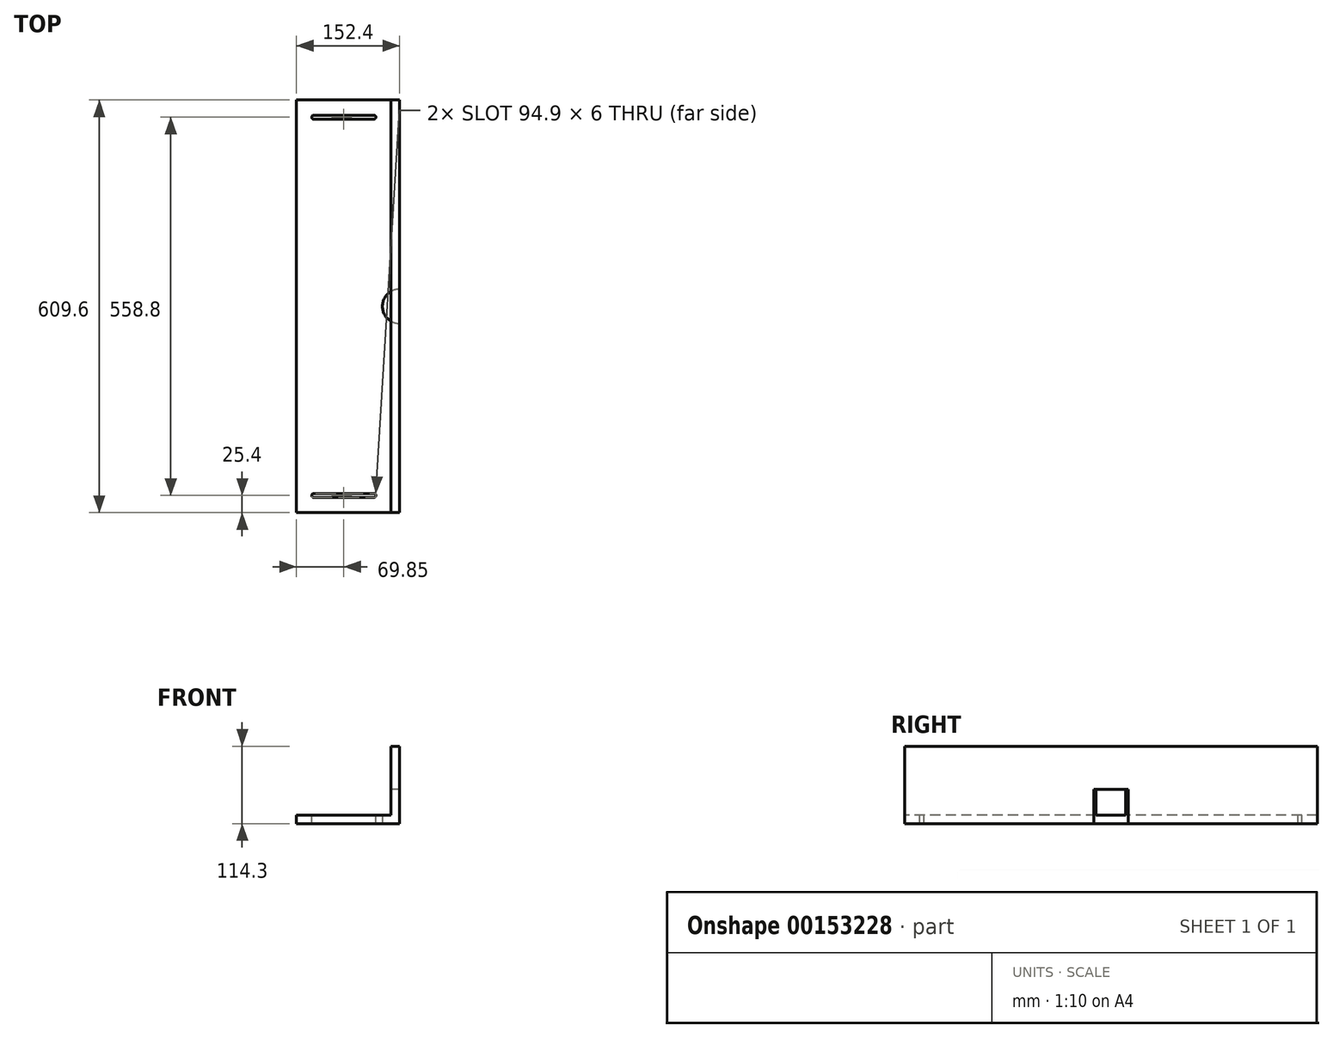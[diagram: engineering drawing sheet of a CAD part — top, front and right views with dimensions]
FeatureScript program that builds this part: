
annotation { "Feature Type Name" : "Feature", "Feature Type Description" : "" }
export const myFeature = defineFeature(function(context is Context, id is Id, definition is map)
    precondition{}
    {
        {
            var Q0;
            Q0=qCreatedBy(makeId("Top.planeOp"),FACE);
            var sketch = newSketch(context, id + "F0", { "sketchPlane" : qUnion([Q0])});
            skLineSegment(sketch, "E0.bottom", {"start": v(-152.4, 304.8) * mm, "end": v(0, 304.8) * mm});
            skLineSegment(sketch, "E0.top", {"start": v(-152.4, -304.8) * mm, "end": v(0, -304.8) * mm});
            skLineSegment(sketch, "E0.left", {"start": v(-152.4, 304.8) * mm, "end": v(-152.4, -304.8) * mm});
            skLineSegment(sketch, "E1", {"start": v(0, 304.8) * mm, "end": v(0, -304.8) * mm});
            skSolve(sketch);
        }
        {
            var Q0;
            Q0=makeQuery(id+"F0.imprint","IMPRINT",FACE,{"disambiguationData":[TD([[makeQuery(id+"F0.imprint","IMPRINT",EDGE,{"derivedFrom":sQuery(id+"F0.wireOp",EDGE,"E0.bottom")}),-1.0]])]});
            extrude(context, id + "F1", {"entities" : qUnion([Q0]), "depth" : 12.7 * mm});
        }
        {
            var Q0;
            Q0=makeQuery(id+"F1.opExtrude","CAP_FACE",FACE,{"disambiguationData":[OSD([sQuery(id+"F0.wireOp",EDGE,"E0.bottom"),sQuery(id+"F0.wireOp",EDGE,"E0.top"),sQuery(id+"F0.wireOp",EDGE,"E0.left"),sQuery(id+"F0.wireOp",EDGE,"E0.right"),sQuery(id+"F0.wireOp",EDGE,"2Zo1Db0u-jxeq-ltlI-ydCZ-03XNrdQAzi5M"),sQuery(id+"F0.wireOp",EDGE,"4c3afef6-3c96-4deb-abbf-9a2fc886915c.trimOffspring")])],"isStart":false});
            var sketch = newSketch(context, id + "F2", { "sketchPlane" : qUnion([Q0])});
            skLineSegment(sketch, "E2.bottom", {"start": v(0, 304.8) * mm, "end": v(-12.7, 304.8) * mm});
            skLineSegment(sketch, "E2.top", {"start": v(0, -304.8) * mm, "end": v(-12.7, -304.8) * mm});
            skLineSegment(sketch, "E2.left", {"start": v(0, 304.8) * mm, "end": v(0, -304.8) * mm});
            skLineSegment(sketch, "E2.right", {"start": v(-12.7, 304.8) * mm, "end": v(-12.7, -304.8) * mm});
            skSolve(sketch);
        }
        {
            var Q0;
            Q0 = qSketchRegion(id + "F2", true);
            extrude(context, id + "F3", {"entities" : qUnion([Q0]), "operationType" : NewBodyOperationType.ADD, "depth" : 101.6 * mm});
        }
        {
            var Q0;
            Q0=makeQuery(id+"F1.opExtrude","CAP_FACE",FACE,{"disambiguationData":[OSD([sQuery(id+"F0.wireOp",EDGE,"E0.bottom"),sQuery(id+"F0.wireOp",EDGE,"E0.top"),sQuery(id+"F0.wireOp",EDGE,"E0.left"),sQuery(id+"F0.wireOp",EDGE,"E1")])],"isStart":false});
            var sketch = newSketch(context, id + "F4", { "sketchPlane" : qUnion([Q0])});
            skLineSegment(sketch, "E3.bottom", {"start": v(-127, 282.4) * mm, "end": v(-38.1, 282.4) * mm});
            skLineSegment(sketch, "E3.top", {"start": v(-127, 276.4) * mm, "end": v(-38.1, 276.4) * mm});
            skLineSegment(sketch, "E4.bottom", {"start": v(-127, -276.4) * mm, "end": v(-38.1, -276.4) * mm});
            skLineSegment(sketch, "E4.top", {"start": v(-127, -282.4) * mm, "end": v(-38.1, -282.4) * mm});
            skArc(sketch, "E5", {"start": v(-127, 282.4) * mm, "mid": v(-130, 279.4) * mm, "end": v(-127, 276.4) * mm});
            skArc(sketch, "E6", {"start": v(-38.1, 276.4) * mm, "mid": v(-35.1, 279.4) * mm, "end": v(-38.1, 282.4) * mm});
            skArc(sketch, "E7", {"start": v(-127, -276.4) * mm, "mid": v(-130, -279.4) * mm, "end": v(-127, -282.4) * mm});
            skArc(sketch, "E8", {"start": v(-38.1, -282.4) * mm, "mid": v(-35.1, -279.4) * mm, "end": v(-38.1, -276.4) * mm});
            skSolve(sketch);
        }
        {
            var Q0;
            Q0 = qSketchRegion(id + "F4", true);
            extrude(context, id + "F5", {"entities" : qUnion([Q0]), "operationType" : NewBodyOperationType.REMOVE, "oppositeDirection" : true, "depth" : 25 * mm});
        }
        {
            var Q0;
            Q0=makeQuery(id+"F1.opExtrude","CAP_FACE",FACE,{"disambiguationData":[OSD([sQuery(id+"F0.wireOp",EDGE,"E0.bottom"),sQuery(id+"F0.wireOp",EDGE,"E0.top"),sQuery(id+"F0.wireOp",EDGE,"E0.left"),sQuery(id+"F0.wireOp",EDGE,"E1")])],"isStart":true});
            var sketch = newSketch(context, id + "F6", { "sketchPlane" : qUnion([Q0])});
            skCircle(sketch, "E9", {"center": v(0, 0) * mm, "radius": 25.4 * mm});
            skSolve(sketch);
        }
        {
            var Q0;
            Q0 = qSketchRegion(id + "F6", true);
            extrude(context, id + "F7", {"entities" : qUnion([Q0]), "operationType" : NewBodyOperationType.REMOVE, "oppositeDirection" : true, "depth" : 50.8 * mm});
        }
    });
